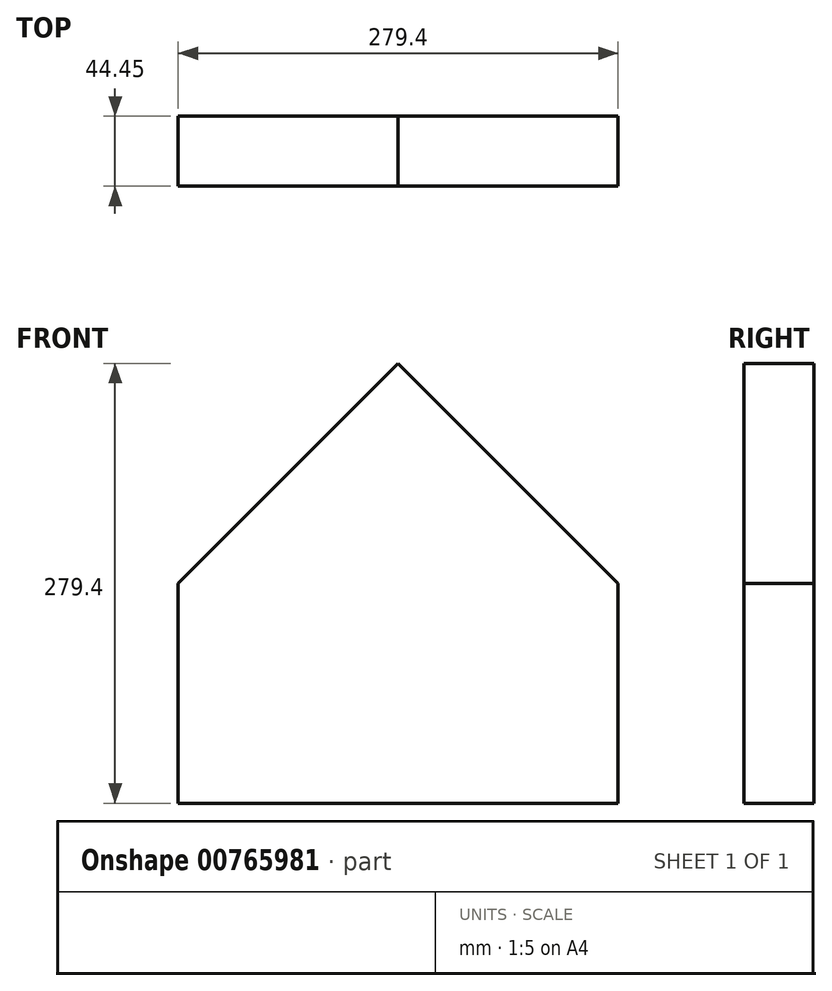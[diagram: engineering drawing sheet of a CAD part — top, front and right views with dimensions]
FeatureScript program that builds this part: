
annotation { "Feature Type Name" : "Feature", "Feature Type Description" : "" }
export const myFeature = defineFeature(function(context is Context, id is Id, definition is map)
    precondition{}
    {
        {
            var Q0;
            Q0=qCreatedBy(makeId("Front.planeOp"),FACE);
            var sketch = newSketch(context, id + "F0", { "sketchPlane" : qUnion([Q0])});
            skLineSegment(sketch, "E0.bottom", {"start": v(0, 0) * mm, "end": v(279.4, 0) * mm});
            skLineSegment(sketch, "E0.left", {"start": v(0, 0) * mm, "end": v(0, 139.7) * mm});
            skLineSegment(sketch, "E0.right", {"start": v(279.4, 0) * mm, "end": v(279.4, 139.7) * mm});
            skLineSegment(sketch, "E1", {"start": v(139.7, 279.4) * mm, "end": v(0, 139.7) * mm});
            skLineSegment(sketch, "E2", {"start": v(139.7, 279.4) * mm, "end": v(279.4, 139.7) * mm});
            skSolve(sketch);
        }
        {
            var Q0;
            Q0=makeQuery(id+"F0.imprint","IMPRINT",FACE,{"disambiguationData":[TD([[makeQuery(id+"F0.imprint","IMPRINT",EDGE,{"derivedFrom":sQuery(id+"F0.wireOp",EDGE,"E0.bottom")}),1.0]])]});
            extrude(context, id + "F1", {"entities" : qUnion([Q0]), "depth" : 44.45 * mm, "offsetDistance" : 25.4 * mm});
        }
    });
